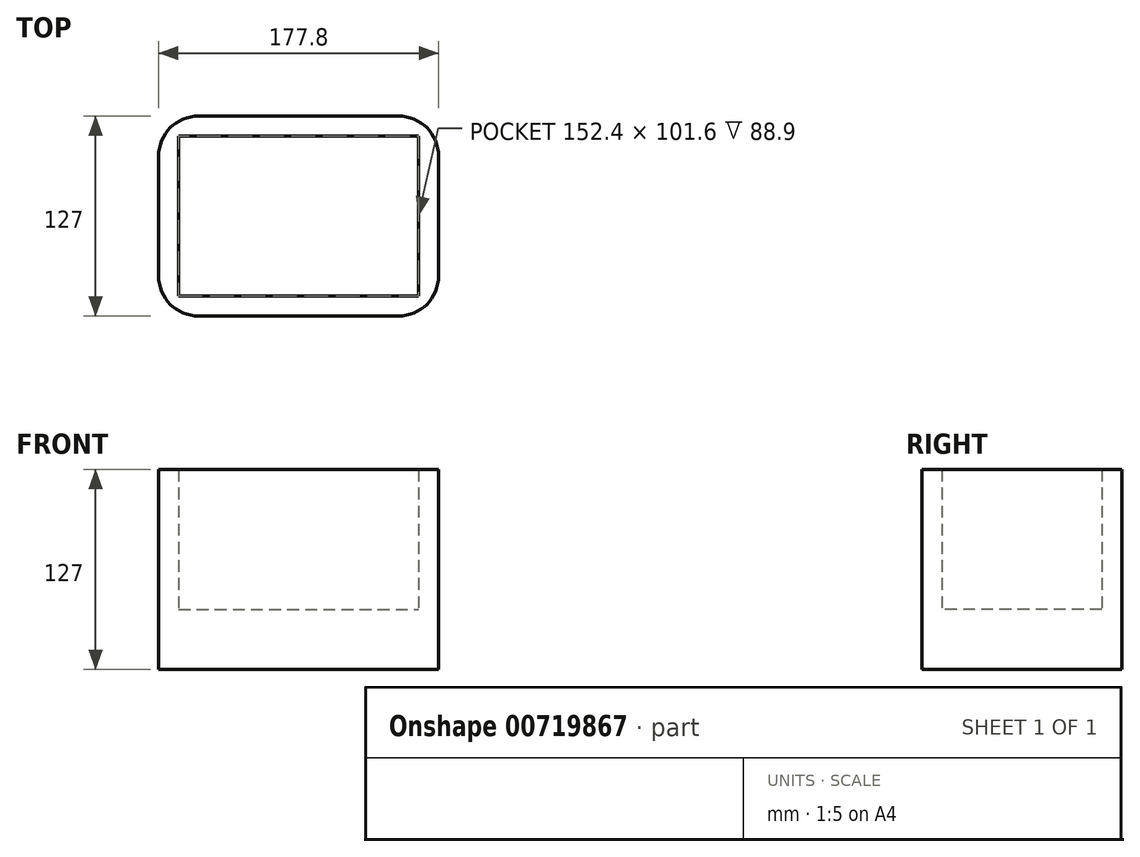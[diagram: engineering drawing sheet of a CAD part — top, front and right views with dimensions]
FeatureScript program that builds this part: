
annotation { "Feature Type Name" : "Feature", "Feature Type Description" : "" }
export const myFeature = defineFeature(function(context is Context, id is Id, definition is map)
    precondition{}
    {
        {
            var Q0;
            Q0=qCreatedBy(makeId("Top.planeOp"),FACE);
            var sketch = newSketch(context, id + "F0", { "sketchPlane" : qUnion([Q0])});
            skLineSegment(sketch, "E0.bottom", {"start": v(0, 0) * mm, "end": v(177.8, 0) * mm});
            skLineSegment(sketch, "E0.top", {"start": v(0, -127) * mm, "end": v(177.8, -127) * mm});
            skLineSegment(sketch, "E0.left", {"start": v(0, 0) * mm, "end": v(0, -127) * mm});
            skLineSegment(sketch, "E0.right", {"start": v(177.8, 0) * mm, "end": v(177.8, -127) * mm});
            skSolve(sketch);
        }
        {
            var Q0;
            Q0=makeQuery(id+"F0.imprint","IMPRINT",FACE,{"disambiguationData":[TD([[makeQuery(id+"F0.imprint","IMPRINT",EDGE,{"derivedFrom":sQuery(id+"F0.wireOp",EDGE,"E0.bottom")}),-1.0]])]});
            extrude(context, id + "F1", {"entities" : qUnion([Q0]), "depth" : 127 * mm, "offsetDistance" : 25.4 * mm});
        }
        {
            var Q0;
            Q0=makeQuery(id+"F1.opExtrude","CAP_FACE",FACE,{"disambiguationData":[OSD([sQuery(id+"F0.wireOp",EDGE,"E0.bottom"),sQuery(id+"F0.wireOp",EDGE,"E0.top"),sQuery(id+"F0.wireOp",EDGE,"E0.left"),sQuery(id+"F0.wireOp",EDGE,"E0.right")])],"isStart":false});
            shell(context, id + "F2", {"entities" : qUnion([Q0]), "thickness" : 12.7 * mm});
        }
        {
            var Q0;
            Q0=makeQuery(id+"F2.opShell","OFFSET_FACE",FACE,{"disambiguationData":[OSD([sQuery(id+"F0.wireOp",EDGE,"E0.bottom"),sQuery(id+"F0.wireOp",EDGE,"E0.top"),sQuery(id+"F0.wireOp",EDGE,"E0.left"),sQuery(id+"F0.wireOp",EDGE,"E0.right")])]});
            extrude(context, id + "F3", {"entities" : qUnion([Q0]), "operationType" : NewBodyOperationType.ADD, "depth" : 25.4 * mm, "offsetDistance" : 25.4 * mm});
        }
        {
            var Q0;
            Q0=makeQuery(id+"F1.opExtrude","SWEPT_EDGE",EDGE,{"disambiguationData":[OSD([sQuery(id+"F0.wireOp",EDGE,"E0.bottom"),sQuery(id+"F0.wireOp",EDGE,"E0.right")])]});
            var Q1;
            Q1=makeQuery(id+"F1.opExtrude","SWEPT_EDGE",EDGE,{"disambiguationData":[OSD([sQuery(id+"F0.wireOp",EDGE,"E0.top"),sQuery(id+"F0.wireOp",EDGE,"E0.right")])]});
            var Q2;
            Q2=makeQuery(id+"F1.opExtrude","SWEPT_EDGE",EDGE,{"disambiguationData":[OSD([sQuery(id+"F0.wireOp",EDGE,"E0.bottom"),sQuery(id+"F0.wireOp",EDGE,"E0.left")])]});
            var Q3;
            Q3=makeQuery(id+"F1.opExtrude","SWEPT_EDGE",EDGE,{"disambiguationData":[OSD([sQuery(id+"F0.wireOp",EDGE,"E0.top"),sQuery(id+"F0.wireOp",EDGE,"E0.left")])]});
            fillet(context, id + "F4", {"entities" : qUnion([Q0, Q1, Q2, Q3]), "radius" : 25.4 * mm, "tangentPropagation" : true, "allowEdgeOverflow" : false});
        }
    });
